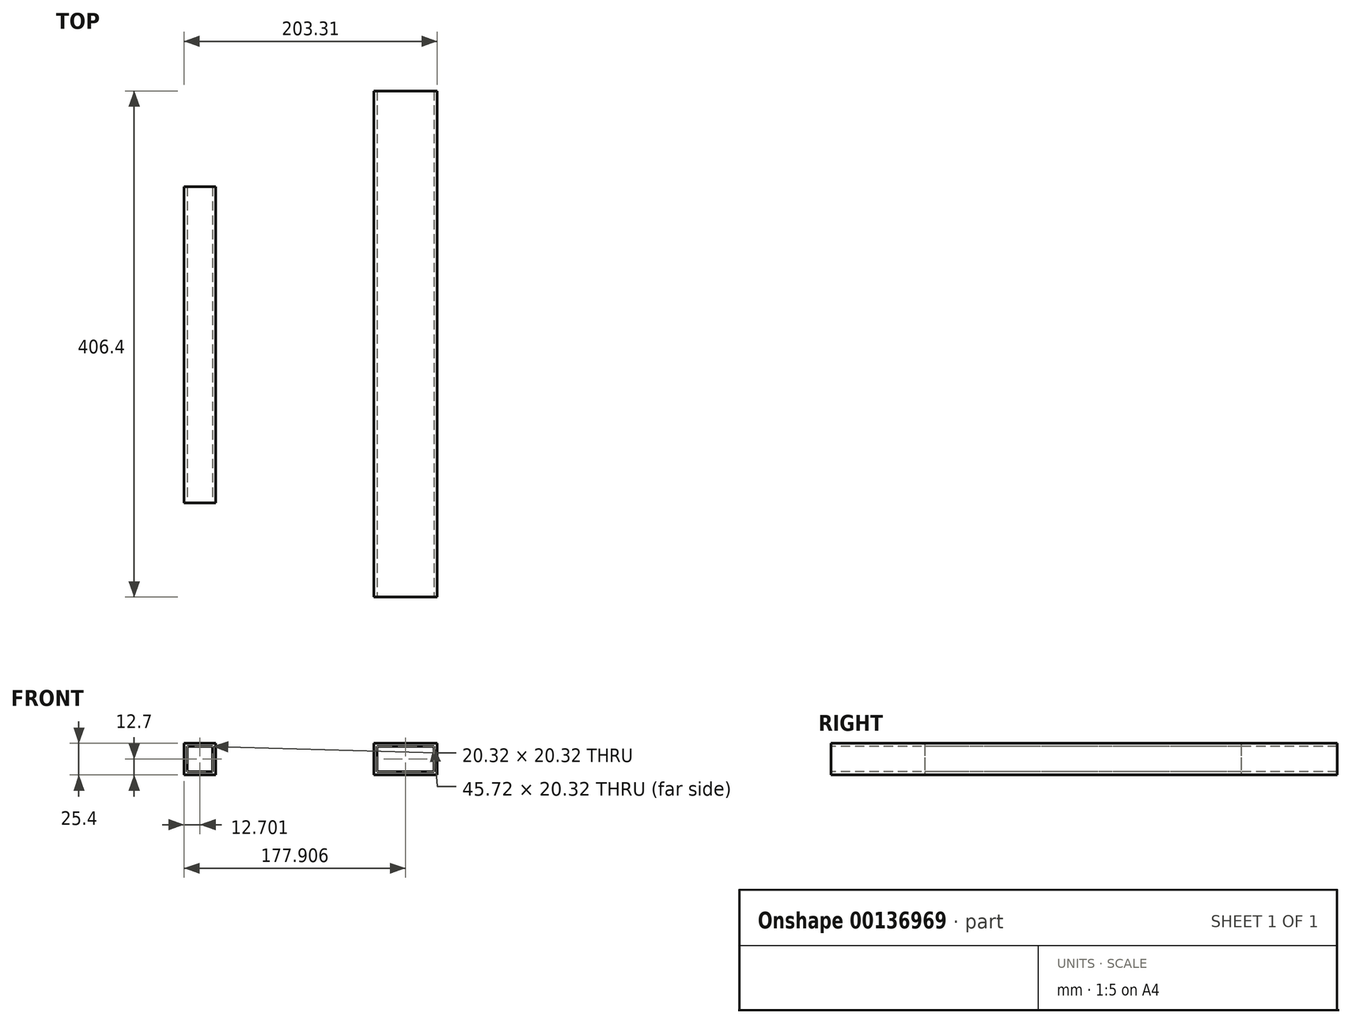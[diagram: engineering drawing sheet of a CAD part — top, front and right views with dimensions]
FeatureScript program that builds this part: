
annotation { "Feature Type Name" : "Feature", "Feature Type Description" : "" }
export const myFeature = defineFeature(function(context is Context, id is Id, definition is map)
    precondition{}
    {
        {
            var Q0;
            Q0=qCreatedBy(makeId("Top.planeOp"),FACE);
            var sketch = newSketch(context, id + "F0", { "sketchPlane" : qUnion([Q0])});
            skLineSegment(sketch, "E0.bottom", {"start": v(-14.11, 167.92) * mm, "end": v(36.69, 167.92) * mm});
            skLineSegment(sketch, "E0.top", {"start": v(-14.11, -238.48) * mm, "end": v(36.69, -238.48) * mm});
            skLineSegment(sketch, "E0.left", {"start": v(-14.11, 167.92) * mm, "end": v(-14.11, -238.48) * mm});
            skLineSegment(sketch, "E0.right", {"start": v(36.69, 167.92) * mm, "end": v(36.69, -238.48) * mm});
            skSolve(sketch);
        }
        {
            var Q0;
            Q0=qSketchRegion(id+"F0",true);
            extrude(context, id + "F1", {"entities" : qUnion([Q0]), "endBound" : BoundingType.SYMMETRIC, "depth" : 25.4 * mm});
        }
        {
            var Q0;
            Q0=makeQuery(id+"F1.opExtrude","SWEPT_FACE",FACE,{"disambiguationData":[OSD([sQuery(id+"F0.wireOp",EDGE,"E0.bottom")])]});
            var Q1;
            Q1=makeQuery(id+"F1.opExtrude","SWEPT_FACE",FACE,{"disambiguationData":[OSD([sQuery(id+"F0.wireOp",EDGE,"E0.top")])]});
            shell(context, id + "F2", {"entities" : qUnion([Q0, Q1]), "thickness" : 2.54 * mm});
        }
        {
            var Q0;
            Q0=qCreatedBy(makeId("Top.planeOp"),FACE);
            var sketch = newSketch(context, id + "F3", { "sketchPlane" : qUnion([Q0])});
            skLineSegment(sketch, "E1.bottom", {"start": v(-166.62, 90.98) * mm, "end": v(-141.22, 90.98) * mm});
            skLineSegment(sketch, "E1.top", {"start": v(-166.62, -163.02) * mm, "end": v(-141.22, -163.02) * mm});
            skLineSegment(sketch, "E1.left", {"start": v(-166.62, 90.98) * mm, "end": v(-166.62, -163.02) * mm});
            skLineSegment(sketch, "E1.right", {"start": v(-141.22, 90.98) * mm, "end": v(-141.22, -163.02) * mm});
            skSolve(sketch);
        }
        {
            var Q0;
            Q0=qSketchRegion(id+"F3",true);
            extrude(context, id + "F4", {"entities" : qUnion([Q0]), "endBound" : BoundingType.SYMMETRIC, "depth" : 25.4 * mm});
        }
        {
            var Q0;
            Q0=makeQuery(id+"F4.opExtrude","SWEPT_FACE",FACE,{"disambiguationData":[OSD([sQuery(id+"F3.wireOp",EDGE,"E1.bottom")])]});
            var Q1;
            Q1=makeQuery(id+"F4.opExtrude","SWEPT_FACE",FACE,{"disambiguationData":[OSD([sQuery(id+"F3.wireOp",EDGE,"E1.top")])]});
            shell(context, id + "F5", {"entities" : qUnion([Q0, Q1]), "thickness" : 2.54 * mm});
        }
    });
